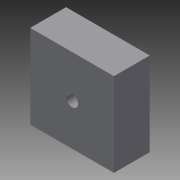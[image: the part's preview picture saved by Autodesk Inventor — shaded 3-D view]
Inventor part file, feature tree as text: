
AUTODESK INVENTOR PART (.ipt)
format: ipt  version: 2015 SP1 (Build 190203100, 203)  size: 79,872 bytes
history: native  units: in
note: dims shown in document units (in); Inventor stores cm internally (conversion verified against a paired STEP export)
features: sketch x2, extrude x1, hole x1, projected_geometry x1
ambient origin geometry x8: Origin, YZ Plane, XZ Plane, XY Plane, X Axis, Y Axis, Z Axis, Center Point
bodies: Solid1 (feature_tree)
feature tree (5):
  extrude  "Extrusion1"  Depth=0.75in
  hole  "Hole1"  [1 undecoded]
  sketch  "Sketch1"  dims[d0=1.75in d1=0.75in]
  sketch  "Sketch2"  dims[d2=1.75in d3=0.0in d4=0.875in d5=0.875in d6=0.25in d7=0.75in d8=0.375in d9=0.25in d10=0.5635in d11=1.0in d12=0.8108in]
  projected_geometry  "Projected Loop1"
note: 1 required parameter value undecoded (feature->parameter linkage not recoverable at this tier; creation-order binding heuristic only, values carry confidence <= 0.55)
